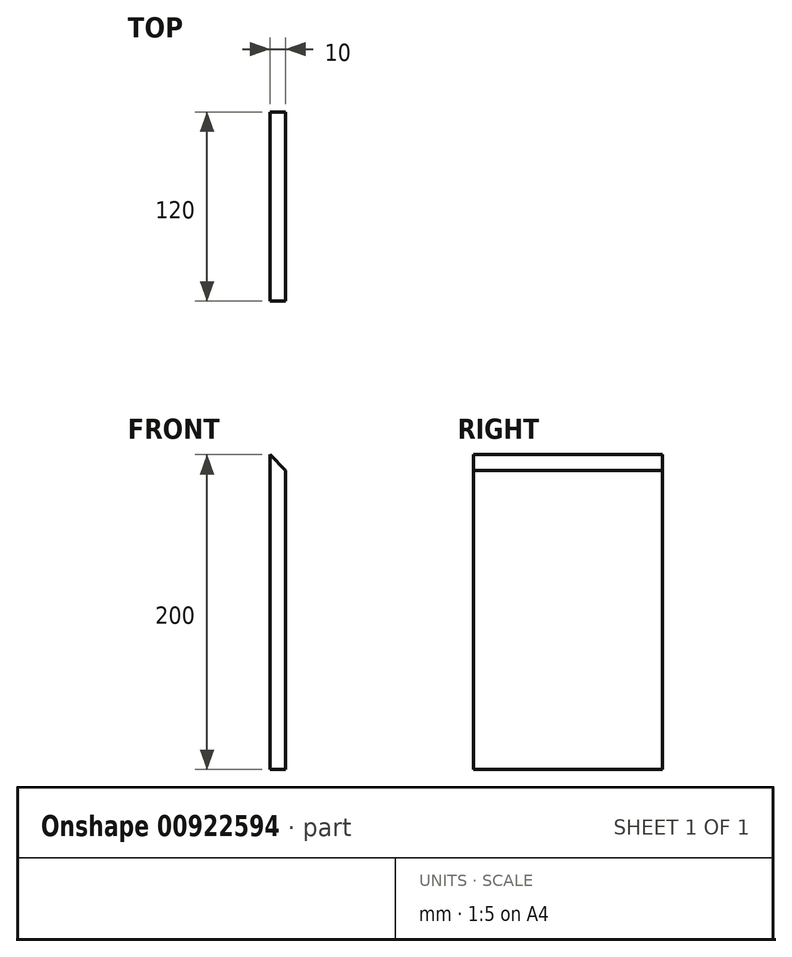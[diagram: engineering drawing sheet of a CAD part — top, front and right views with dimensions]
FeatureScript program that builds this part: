
annotation { "Feature Type Name" : "Feature", "Feature Type Description" : "" }
export const myFeature = defineFeature(function(context is Context, id is Id, definition is map)
    precondition{}
    {
        {
            var Q0;
            Q0=qCreatedBy(makeId("Right.planeOp"),FACE);
            var sketch = newSketch(context, id + "F0", { "sketchPlane" : qUnion([Q0])});
            skLineSegment(sketch, "E0.bottom", {"start": v(60, 100) * mm, "end": v(-60, 100) * mm});
            skLineSegment(sketch, "E0.top", {"start": v(60, -100) * mm, "end": v(-60, -100) * mm});
            skLineSegment(sketch, "E0.left", {"start": v(60, 100) * mm, "end": v(60, -100) * mm});
            skLineSegment(sketch, "E0.right", {"start": v(-60, 100) * mm, "end": v(-60, -100) * mm});
            skPoint(sketch, "E0.middle", {"position": v(0, 0) * mm});
            skSolve(sketch);
        }
        {
            var Q0;
            Q0 = qSketchRegion(id + "F0", true);
            extrude(context, id + "F1", {"entities" : qUnion([Q0]), "depth" : 10 * mm, "offsetDistance" : 25.4 * mm});
        }
        {
            var Q0;
            Q0=makeQuery(id+"F1.opExtrude","CAP_EDGE",EDGE,{"disambiguationData":[OSD([sQuery(id+"F0.wireOp",EDGE,"E0.bottom")])],"isStart":false});
            chamfer(context, id + "F2", {"entities" : qUnion([Q0]), "width" : 10 * mm, "tangentPropagation" : true});
        }
    });
